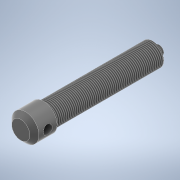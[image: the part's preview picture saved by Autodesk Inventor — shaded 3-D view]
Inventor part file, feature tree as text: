
AUTODESK INVENTOR PART (.ipt)
format: ipt  version: 2021 (Build 250183000, 183)  size: 131,072 bytes
history: native  units: mm
features: extrude x4, sketch x4, other x1, chamfer x1, thread x1
ambient origin geometry x8: Origin, YZ Plane, XZ Plane, XY Plane, X Axis, Y Axis, Z Axis, Center Point
bodies: Body1 (feature_tree)
feature tree (11):
  other  "Sólido1"
  extrude  "Extrusão1"  Depth=240.0mm TaperAngle=0.0deg
  extrude  "Extrusão2"  Depth=240.0mm TaperAngle=0.0deg
  chamfer  "Chanfro1"  Distance=10.0mm Angle=45.0deg
  thread  "Rosca1"  [1 undecoded]
  extrude  "Extrusão3"  TaperAngle=0.0deg  [1 undecoded]
  extrude  "Extrusão4"  Depth=15.0mm TaperAngle=0.0deg
  sketch  "Esboço1"  dims[d0=50.0mm d1=240.0mm d2=0.0mm]
  sketch  "Esboço2"  dims[d3=60.0mm d4=50.0mm d5=0.0mm d6=10.0mm d7=2.0mm d8=45.0deg d9=240.0mm d10=0.0mm]
  sketch  "Esboço3"  dims[d11=20.0mm d12=0.0mm d13=0.0mm]
  sketch  "Esboço4"  dims[d14=20.0mm d15=15.0mm d16=0.0mm]
note: 2 required parameter values undecoded (feature->parameter linkage not recoverable at this tier; creation-order binding heuristic only, values carry confidence <= 0.55)
